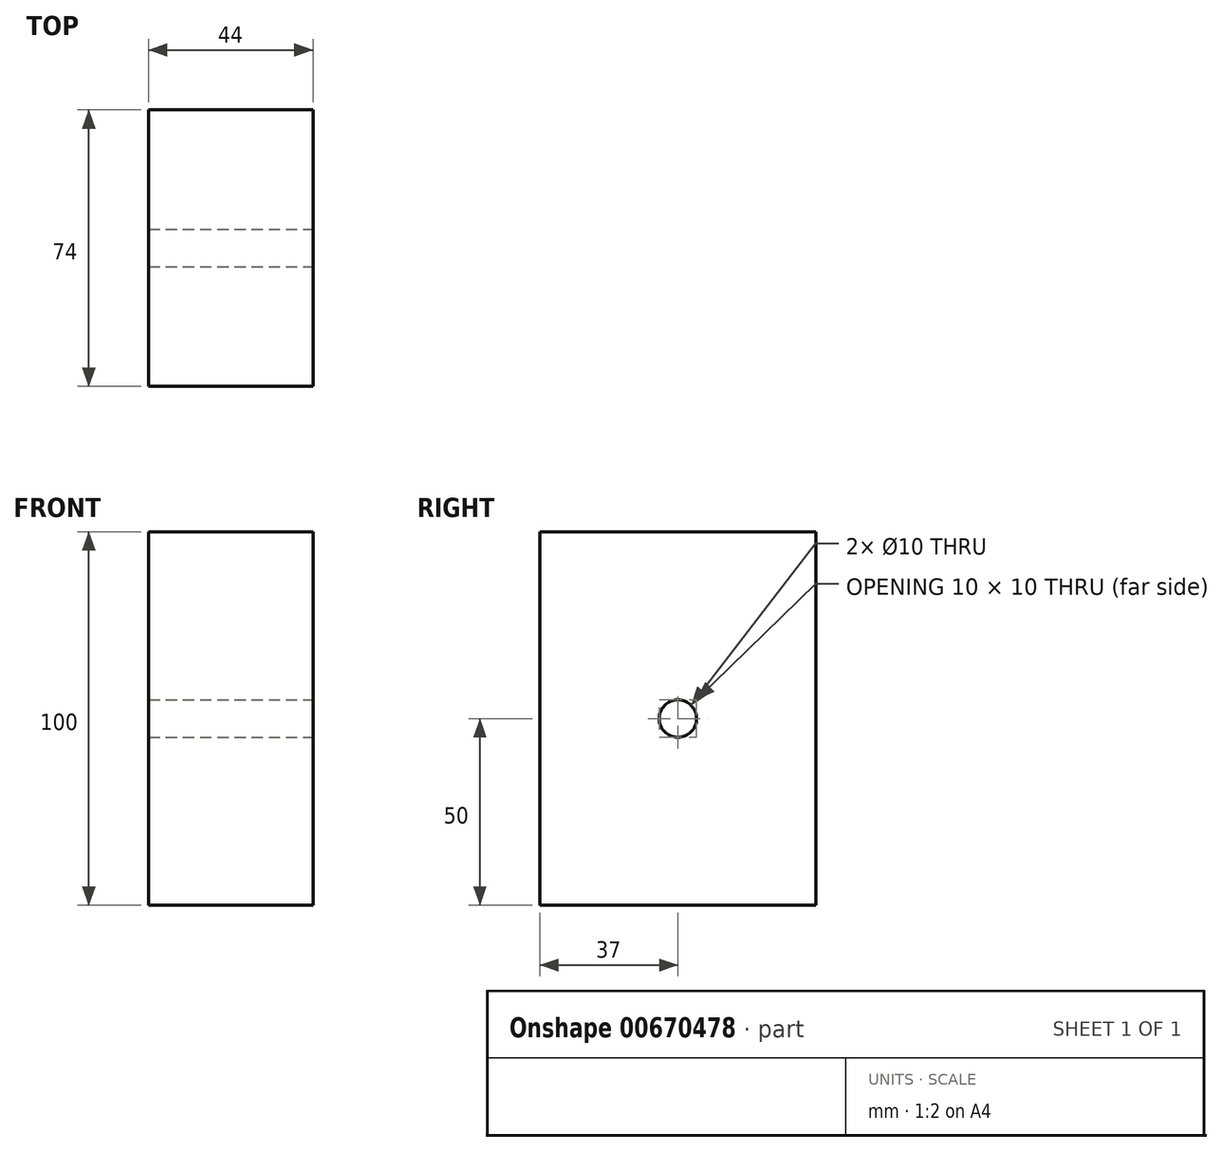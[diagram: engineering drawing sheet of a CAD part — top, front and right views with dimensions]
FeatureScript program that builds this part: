
annotation { "Feature Type Name" : "Feature", "Feature Type Description" : "" }
export const myFeature = defineFeature(function(context is Context, id is Id, definition is map)
    precondition{}
    {
        {
            var Q0;
            Q0=qCreatedBy(makeId("Top.planeOp"),FACE);
            var sketch = newSketch(context, id + "F0", { "sketchPlane" : qUnion([Q0])});
            skLineSegment(sketch, "E0.bottom", {"start": v(22, -37) * mm, "end": v(-22, -37) * mm});
            skLineSegment(sketch, "E0.top", {"start": v(22, 37) * mm, "end": v(-22, 37) * mm});
            skLineSegment(sketch, "E0.left", {"start": v(22, -37) * mm, "end": v(22, 37) * mm});
            skLineSegment(sketch, "E0.right", {"start": v(-22, -37) * mm, "end": v(-22, 37) * mm});
            skPoint(sketch, "E0.middle", {"position": v(0, 0) * mm});
            skSolve(sketch);
        }
        {
            var Q0;
            Q0=qSketchRegion(id+"F0",true);
            extrude(context, id + "F1", {"entities" : qUnion([Q0]), "depth" : 100 * mm, "offsetDistance" : 25.4 * mm});
        }
        {
            var Q0;
            Q0=makeQuery(id+"F1.opExtrude","SWEPT_FACE",FACE,{"disambiguationData":[OSD([sQuery(id+"F0.wireOp",EDGE,"E0.left")])]});
            var sketch = newSketch(context, id + "F2", { "sketchPlane" : qUnion([Q0])});
            skCircle(sketch, "E1", {"center": v(0, 50) * mm, "radius": 5 * mm});
            skLineSegment(sketch, "E2", {"start": v(-37, 50) * mm, "end": v(37, 50) * mm, "construction": true});
            skSolve(sketch);
        }
        {
            var Q0;
            Q0 = qSketchRegion(id + "F2", true);
            extrude(context, id + "F3", {"entities" : qUnion([Q0]), "operationType" : NewBodyOperationType.REMOVE, "endBound" : BoundingType.THROUGH_ALL, "oppositeDirection" : true, "depth" : 25.4 * mm, "offsetDistance" : 25.4 * mm});
        }
    });
